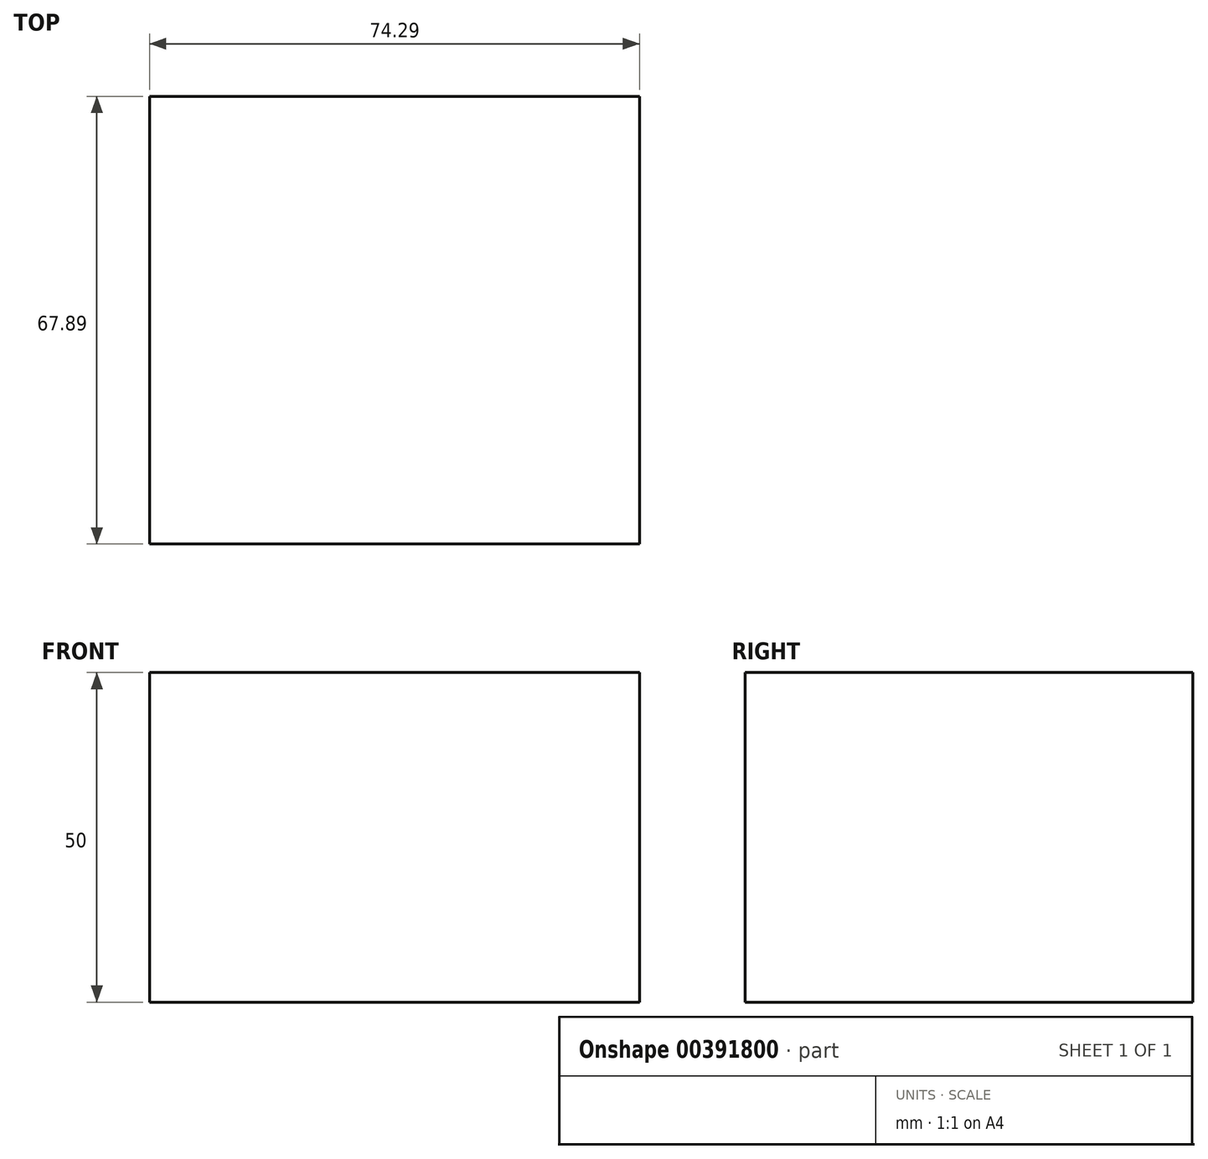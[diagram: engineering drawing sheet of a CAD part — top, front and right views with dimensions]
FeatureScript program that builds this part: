
annotation { "Feature Type Name" : "Feature", "Feature Type Description" : "" }
export const myFeature = defineFeature(function(context is Context, id is Id, definition is map)
    precondition{}
    {
        {
            var Q0;
            Q0=qCreatedBy(makeId("Top.planeOp"),FACE);
            var sketch = newSketch(context, id + "F0", { "sketchPlane" : qUnion([Q0])});
            skLineSegment(sketch, "E0.bottom", {"start": v(0, 0) * mm, "end": v(74.3, 0) * mm});
            skLineSegment(sketch, "E0.top", {"start": v(0, -67.9) * mm, "end": v(74.3, -67.9) * mm});
            skLineSegment(sketch, "E0.left", {"start": v(0, 0) * mm, "end": v(0, -67.9) * mm});
            skLineSegment(sketch, "E0.right", {"start": v(74.3, 0) * mm, "end": v(74.3, -67.9) * mm});
            skSolve(sketch);
        }
        {
            var Q0;
            Q0=makeQuery(id+"F0.imprint","IMPRINT",FACE,{"disambiguationData":[TD([[makeQuery(id+"F0.imprint","IMPRINT",EDGE,{"derivedFrom":sQuery(id+"F0.wireOp",EDGE,"E0.bottom")}),-1.0]])]});
            extrude(context, id + "F1", {"entities" : qUnion([Q0]), "oppositeDirection" : true, "depth" : 50 * mm});
        }
    });
